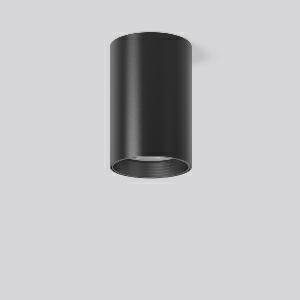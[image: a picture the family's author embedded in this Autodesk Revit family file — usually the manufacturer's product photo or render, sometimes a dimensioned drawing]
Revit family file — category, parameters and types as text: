
# Revit family: heledon_maxi_a_931248_003_2_0cca
name_source: partatom
category: Lighting Fixtures
units: mm (PartAtom-declared; Revit-internal decimal feet)

## family parameters
Cut with Voids When Loaded = No
Host = Face
Light Source = No
Part Type = Normal
Room Calculation Point = No
Round Connector Dimension = Use Diameter
Shared = No

## types (1)
- HELEDON maxi A (1 x LED Modul 927 bakery, 2950 lm, 2700)
    Apparent Load = 33 VA
    Approval mark = CE
    CIE Flux Codes = 97 100 100 100 100
    Color Rendering = 90
    Color Temperature = 2700
    Default Elevation = 1800 mm
    Description = Series: HELEDON maxi
Cylindrical surface-mounted downlight. Housing: die-cast aluminium, powder-coated. Internal ceiling frame polycarbonate with bayonet mounting. Black plastic ring and recessed LED to prevent glare from the side. Optical assembly with lens made of plastic (polycarbonate) for the best homogeneous light distribution - can be changed without tools. Special LED for illumination of pastries included. Suitable for Ceiling mounting. Easy installation with a separate ceiling frame with bayonet mounting and plug connection. Driver integrated. Connected via plug-in connector. High quality converter without flickering and stroboscopic effect. The following accessories can be mounted without use of tools: interchangeable lenses, decorative glasses, honeycomb louvre, clear and frosted diffusers, white interchangeable plastic ring. 
Colour: deep black, matt (RAL 9005)
Diameter: 123 mm
Height: 183 mm
Lamp: LED
Socket: without socket
Colour temperature: bakery
Colour rendering index (CRI): 97
System power: 33 W
Rated luminous flux: 2950 lm
Luminous efficiency: 89 lm/W
Control gear: Regulated power supply
Protection class: I
Type of protection: IP 20
    Height = 183 mm
    Lamp = 1 x LED Modul 927 bakery
    Lamp Light Flux = 2950 lm
    Lamp count = 1
    Length = 123 mm
    Lifetime = 50000 h
    Luminous efficacy = 89 lm/W
    Manufacturer = RZB
    ModVariant = No
    Model = 931248.003.2
    Mounting Place = Ceiling
    Mounting Type = Surface mounted
    Number of Poles = 1
    OnlyDefault = Yes
    Power Factor = 1
    Product Name = HELEDON maxi A
    Product group = Surface mounted downlights
    ProductGroupID = 302
    Protection Class = Protection class I
    Protection Degree = IP 20
    RLX_Detail_Level = 1
    RLX_Emergency_Light_Flux = 0 lm
    RLX_Emergency_Type = 0
    RLX_Emergency_Type_DB = No
    RlxData = <blob elided: 97553 chars, md5=f698e9d5>
    Socket = socket
    Standby Power = 0 W
    System Light Flux = 2950 lm
    System Power = 33 W
    Type Comments = Product without accessories
    Type Image = 931193.003.jpg
    URL = http://relux.com
    VarID = ---
    Voltage = 230 V
    Voltage Range = 220-240 V
    Weight = 0.00 kg
    Width = 0 mm  [stored 0 ft]

note: [stored X ft] marks values corroborated as IEEE doubles in the binary element streams (Revit-internal decimal feet)

## geometry (parser evidence)
native form markers: Blend x4, Sweep x10
no freeform markers — native parametric forms only
